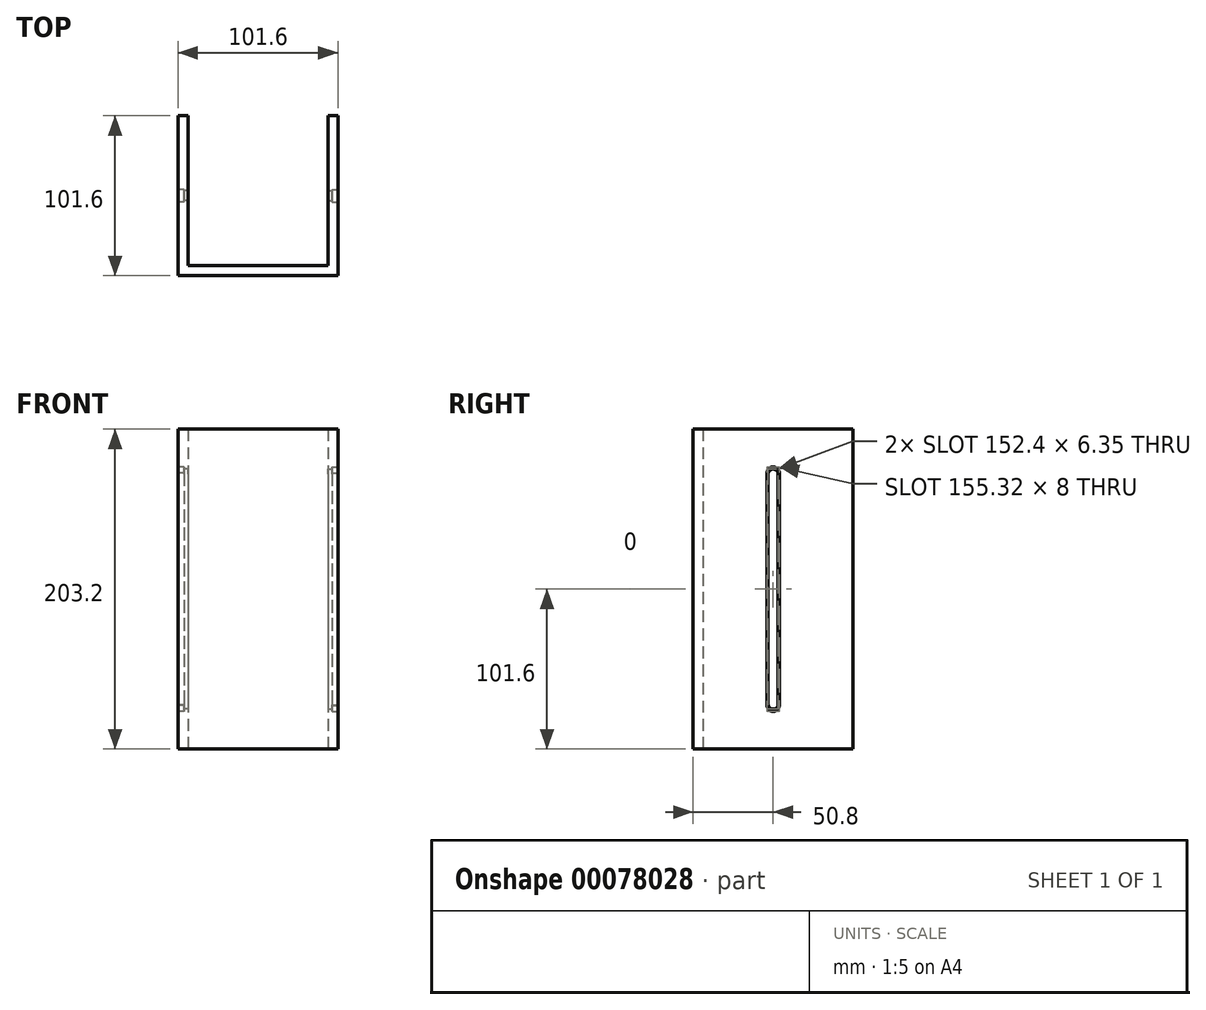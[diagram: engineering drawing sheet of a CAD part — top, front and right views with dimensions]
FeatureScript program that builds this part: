
annotation { "Feature Type Name" : "Feature", "Feature Type Description" : "" }
export const myFeature = defineFeature(function(context is Context, id is Id, definition is map)
    precondition{}
    {
        {
            var Q0;
            Q0=qCreatedBy(makeId("Top.planeOp"),FACE);
            var sketch = newSketch(context, id + "F0", { "sketchPlane" : qUnion([Q0])});
            skLineSegment(sketch, "E0", {"start": v(44.45, 6.35) * mm, "end": v(44.45, 101.6) * mm});
            skLineSegment(sketch, "E1", {"start": v(44.45, 101.6) * mm, "end": v(50.8, 101.6) * mm});
            skLineSegment(sketch, "E2", {"start": v(50.8, 101.6) * mm, "end": v(50.8, 0) * mm});
            skLineSegment(sketch, "E3", {"start": v(0, 6.35) * mm, "end": v(0, 0) * mm});
            skLineSegment(sketch, "E4", {"start": v(0, 6.35) * mm, "end": v(44.45, 6.35) * mm});
            skLineSegment(sketch, "E5", {"start": v(0, 0) * mm, "end": v(50.8, 0) * mm});
            skSolve(sketch);
        }
        {
            var Q0;
            Q0 = qSketchRegion(id + "F0", true);
            extrude(context, id + "F1", {"entities" : qUnion([Q0]), "endBound" : BoundingType.SYMMETRIC, "depth" : 203.2 * mm});
        }
        {
            var Q0;
            Q0=qCreatedBy(makeId("Right.planeOp"),FACE);
            var sketch = newSketch(context, id + "F2", { "sketchPlane" : qUnion([Q0])});
            skLineSegment(sketch, "E6.bottom", {"start": v(101.6, -101.6) * mm, "end": v(0, -101.6) * mm, "construction": true});
            skLineSegment(sketch, "E6.top", {"start": v(101.6, 101.6) * mm, "end": v(0, 101.6) * mm, "construction": true});
            skLineSegment(sketch, "E6.left", {"start": v(101.6, -101.6) * mm, "end": v(101.6, 101.6) * mm, "construction": true});
            skLineSegment(sketch, "E6.right", {"start": v(0, -101.6) * mm, "end": v(0, 101.6) * mm, "construction": true});
            skLineSegment(sketch, "E7.bottom", {"start": v(53.98, -76.2) * mm, "end": v(47.63, -76.2) * mm});
            skLineSegment(sketch, "E7.top", {"start": v(53.97, 76.2) * mm, "end": v(47.62, 76.2) * mm});
            skLineSegment(sketch, "E7.left", {"start": v(53.98, -76.2) * mm, "end": v(53.97, 76.2) * mm});
            skLineSegment(sketch, "E7.right", {"start": v(47.63, -76.2) * mm, "end": v(47.62, 76.2) * mm});
            skLineSegment(sketch, "E8", {"start": v(50.8, -76.2) * mm, "end": v(50.8, 76.2) * mm, "construction": true});
            skArc(sketch, "E9", {"start": v(47.63, -73.02) * mm, "mid": v(50.8, -76.2) * mm, "end": v(53.98, -73.02) * mm});
            skLineSegment(sketch, "E10", {"start": v(53.97, -73.02) * mm, "end": v(47.62, -73.03) * mm, "construction": true});
            skArc(sketch, "E11", {"start": v(53.98, 73.02) * mm, "mid": v(50.8, 76.2) * mm, "end": v(47.63, 73.03) * mm});
            skSolve(sketch);
        }
        {
            var Q0;
            {var subQ0=sQuery(id+"F2.wireOp",EDGE,"E9");var subQ1=sQuery(id+"F2.wireOp",EDGE,"E7.left");var subQ2=makeQuery(id+"F2.imprint","INTERSECT",VERTEX,{"derivedFrom":[subQ1,subQ0]});Q0=makeQuery(id+"F2.imprint","IMPRINT",FACE,{"disambiguationData":[TD([[makeQuery(id+"F2.imprint","IMPRINT",EDGE,{"disambiguationData":[TD([[subQ2,-1.0]])],"derivedFrom":subQ1}),1.0]])]});}
            extrude(context, id + "F3", {"entities" : qUnion([Q0]), "operationType" : NewBodyOperationType.REMOVE, "endBound" : BoundingType.THROUGH_ALL, "oppositeDirection" : true, "depth" : 25.4 * mm, "hasSecondDirection" : true, "secondDirectionBound" : SecondDirectionBoundingType.THROUGH_ALL, "secondDirectionOppositeDirection" : false, "secondDirectionDepth" : 25.4 * mm});
        }
        {
            var Q0;
            Q0=makeQuery(id+"F1.opExtrude","SWEPT_FACE",FACE,{"disambiguationData":[OSD([sQuery(id+"F0.wireOp",EDGE,"E2")])]});
            var sketch = newSketch(context, id + "F4", { "sketchPlane" : qUnion([Q0])});
            skArc(sketch, "E12", {"start": v(54.8, 73.78) * mm, "mid": v(50.74, 77.66) * mm, "end": v(46.8, 73.66) * mm});
            skArc(sketch, "E13", {"start": v(46.8, -73.74) * mm, "mid": v(50.89, -77.66) * mm, "end": v(54.8, -73.57) * mm});
            skLineSegment(sketch, "E14", {"start": v(46.8, 73.66) * mm, "end": v(46.8, -73.74) * mm});
            skLineSegment(sketch, "E15", {"start": v(54.8, 73.78) * mm, "end": v(54.8, -73.57) * mm});
            skLineSegment(sketch, "E16", {"start": v(50.8, 73.66) * mm, "end": v(50.8, -73.66) * mm, "construction": true});
            skSolve(sketch);
        }
        {
            var Q0;
            Q0 = qSketchRegion(id + "F4", true);
            extrude(context, id + "F5", {"entities" : qUnion([Q0]), "operationType" : NewBodyOperationType.REMOVE, "oppositeDirection" : true, "depth" : 3.8 * mm});
        }
        {
            var Q0;
            Q0=makeQuery(id+"F1.opExtrude","SWEPT_BODY",BODY,{"disambiguationData":[OSD([sQuery(id+"F0.wireOp",EDGE,"E0"),sQuery(id+"F0.wireOp",EDGE,"E1"),sQuery(id+"F0.wireOp",EDGE,"E2"),sQuery(id+"F0.wireOp",EDGE,"E3"),sQuery(id+"F0.wireOp",EDGE,"E4"),sQuery(id+"F0.wireOp",EDGE,"E5")])]});
            var Q1;
            Q1=qCreatedBy(makeId("Right.planeOp"),FACE);
            mirror(context, id + "F6", {"operationType" : NewBodyOperationType.ADD, "entities" : qUnion([Q0]), "mirrorPlane" : qUnion([Q1])});
        }
    });
